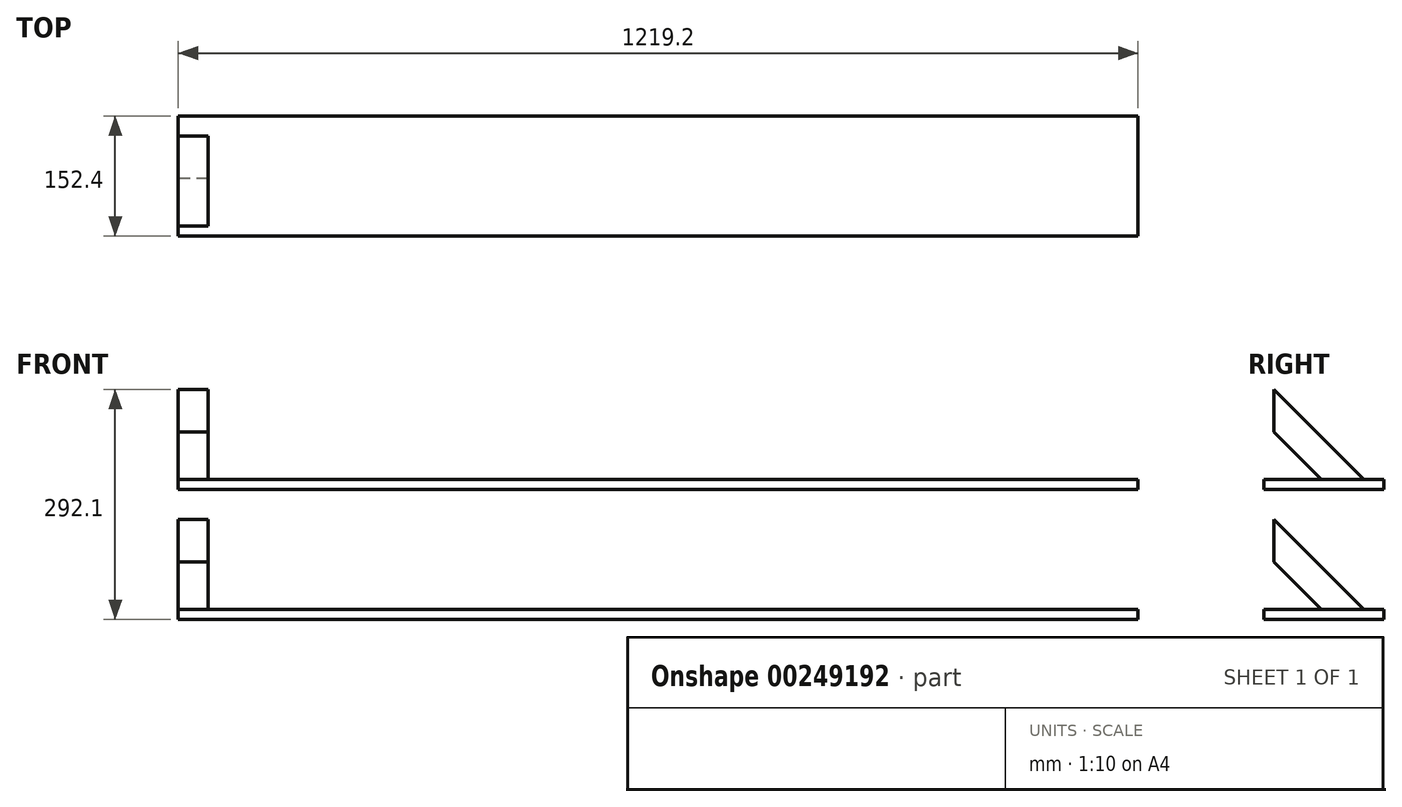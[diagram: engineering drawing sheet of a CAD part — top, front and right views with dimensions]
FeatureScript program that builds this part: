
annotation { "Feature Type Name" : "Feature", "Feature Type Description" : "" }
export const myFeature = defineFeature(function(context is Context, id is Id, definition is map)
    precondition{}
    {
        {
            var Q0;
            Q0=qCreatedBy(makeId("Right.planeOp"),FACE);
            var sketch = newSketch(context, id + "F0", { "sketchPlane" : qUnion([Q0])});
            skLineSegment(sketch, "E0.bottom", {"start": v(0, 0) * mm, "end": v(152.4, 0) * mm});
            skLineSegment(sketch, "E0.top", {"start": v(0, 12.7) * mm, "end": v(152.4, 12.7) * mm});
            skLineSegment(sketch, "E0.left", {"start": v(0, 0) * mm, "end": v(0, 12.7) * mm});
            skLineSegment(sketch, "E0.right", {"start": v(152.4, 0) * mm, "end": v(152.4, 12.7) * mm});
            skLineSegment(sketch, "E1.bottom", {"start": v(0, 0) * mm, "end": v(12.7, 0) * mm});
            skLineSegment(sketch, "E1.top", {"start": v(0, -152.4) * mm, "end": v(12.7, -152.4) * mm});
            skLineSegment(sketch, "E1.left", {"start": v(0, 0) * mm, "end": v(0, -152.4) * mm});
            skLineSegment(sketch, "E1.right", {"start": v(12.7, 0) * mm, "end": v(12.7, -152.4) * mm});
            skLineSegment(sketch, "E2.bottom", {"start": v(0, 12.7) * mm, "end": v(12.7, 12.7) * mm});
            skLineSegment(sketch, "E2.top", {"start": v(0, 165.1) * mm, "end": v(12.7, 165.1) * mm});
            skLineSegment(sketch, "E2.left", {"start": v(0, 12.7) * mm, "end": v(0, 165.1) * mm});
            skLineSegment(sketch, "E2.right", {"start": v(12.7, 12.7) * mm, "end": v(12.7, 165.1) * mm});
            skLineSegment(sketch, "E3.bottom", {"start": v(0, 165.1) * mm, "end": v(152.4, 165.1) * mm});
            skLineSegment(sketch, "E3.top", {"start": v(0, 177.8) * mm, "end": v(152.4, 177.8) * mm});
            skLineSegment(sketch, "E3.left", {"start": v(0, 165.1) * mm, "end": v(0, 177.8) * mm});
            skLineSegment(sketch, "E3.right", {"start": v(152.4, 165.1) * mm, "end": v(152.4, 177.8) * mm});
            skLineSegment(sketch, "E4.bottom", {"start": v(0, 177.8) * mm, "end": v(12.7, 177.8) * mm});
            skLineSegment(sketch, "E4.top", {"start": v(0, 330.2) * mm, "end": v(12.7, 330.2) * mm});
            skLineSegment(sketch, "E4.left", {"start": v(0, 177.8) * mm, "end": v(0, 330.2) * mm});
            skLineSegment(sketch, "E4.right", {"start": v(12.7, 177.8) * mm, "end": v(12.7, 330.2) * mm});
            skLineSegment(sketch, "E5", {"start": v(12.7, 292.1) * mm, "end": v(127, 177.8) * mm});
            skLineSegment(sketch, "E6", {"start": v(127, 177.8) * mm, "end": v(73.12, 177.8) * mm});
            skLineSegment(sketch, "E7", {"start": v(73.12, 177.8) * mm, "end": v(12.7, 238.22) * mm});
            skLineSegment(sketch, "E8", {"start": v(12.7, 238.22) * mm, "end": v(12.7, 292.1) * mm});
            skLineSegment(sketch, "E9", {"start": v(127, 12.7) * mm, "end": v(12.7, 127) * mm});
            skLineSegment(sketch, "E10", {"start": v(73.12, 12.7) * mm, "end": v(12.7, 73.12) * mm});
            skSolve(sketch);
        }
        {
            var Q0;
            {var subQ1=sQuery(id+"F0.wireOp",EDGE,"E4.bottom");Q0=makeQuery(id+"F0.imprint","IMPRINT",FACE,{"disambiguationData":[TD([[makeQuery(id+"F0.imprint","IMPRINT",EDGE,{"derivedFrom":subQ1}),1.0]])]});}
            var Q1;
            {var subQ6=sQuery(id+"F0.wireOp",EDGE,"E3.left");Q1=makeQuery(id+"F0.imprint","IMPRINT",FACE,{"disambiguationData":[TD([[makeQuery(id+"F0.imprint","IMPRINT",EDGE,{"derivedFrom":subQ6}),-1.0]])]});}
            var Q2;
            Q2=makeQuery(id+"F0.imprint","IMPRINT",FACE,{"disambiguationData":[TD([[makeQuery(id+"F0.imprint","IMPRINT",EDGE,{"derivedFrom":sQuery(id+"F0.wireOp",EDGE,"E2.bottom")}),1.0]])]});
            var Q3;
            Q3=makeQuery(id+"F0.imprint","IMPRINT",FACE,{"disambiguationData":[TD([[makeQuery(id+"F0.imprint","IMPRINT",EDGE,{"derivedFrom":sQuery(id+"F0.wireOp",EDGE,"E0.bottom")}),1.0]])]});
            var Q4;
            Q4=makeQuery(id+"F0.imprint","IMPRINT",FACE,{"disambiguationData":[TD([[makeQuery(id+"F0.imprint","IMPRINT",EDGE,{"derivedFrom":sQuery(id+"F0.wireOp",EDGE,"E1.bottom")}),-1.0]])]});
            extrude(context, id + "F1", {"entities" : qUnion([Q0, Q1, Q2, Q3, Q4]), "depth" : 1219.2 * mm});
        }
        {
            var Q0;
            Q0=makeQuery(id+"F0.imprint","IMPRINT",FACE,{"disambiguationData":[TD([[makeQuery(id+"F0.imprint","IMPRINT",EDGE,{"derivedFrom":sQuery(id+"F0.wireOp",EDGE,"E5")}),-1.0]])]});
            var Q1;
            {var subQ0=sQuery(id+"F0.wireOp",EDGE,"E9");Q1=makeQuery(id+"F0.imprint","IMPRINT",FACE,{"disambiguationData":[TD([[makeQuery(id+"F0.imprint","IMPRINT",EDGE,{"derivedFrom":subQ0}),1.0]])]});}
            extrude(context, id + "F2", {"entities" : qUnion([Q0, Q1]), "operationType" : NewBodyOperationType.ADD, "depth" : 38.1 * mm});
        }
    });
